# Revit family: MA551
name_source: partatom
category: Communication Devices
revit_build: Autodesk Revit 2018 (Build: 20170223_1515(x64)
units: mm (PartAtom-declared; Revit-internal decimal feet)

## family parameters
Always vertical = Yes
Cut with Voids When Loaded = No
Maintain Annotation Orientation = No
Part Type = Normal
Room Calculation Point = No
Round Connector Dimension = Use Diameter
Shared = No
Work Plane-Based = No

## types (1)
- MA551
    CONNECTIVITY - Input Terminals - Data = USB 2.0 x 2 (5V/2A, FW), USB Type B (Software)
    CONNECTIVITY - Input Terminals - Digital = HDMI 2.0 x 2, DP 1.4 x 2.4
    CONNECTIVITY - Input Terminals - External Control = LAN (100Mbit), 3.5mm Mini Jack IR Remote, RS-232C
    CONNECTIVITY - Output Terminals - Audio = 3.5mm Mini Jack, External Speaker Jack (15W x 2)
    CONNECTIVITY - Output Terminals - Digital = HDMI x 1, DisplayPort x 1
    CONNECTIVITY - Output Terminals - External Control = LAN (100Mbit)
    Description = NEC MultiSync MA Series Large Format Displays
    ENVIRONMENTAL CONDITIONS- Operating Altitude" = 3000m (9843ft
    ENVIRONMENTAL CONDITIONS- Operating Humidity = 20-80%
    ENVIRONMENTAL CONDITIONS- Operating Temperature = 0 to 40C
    LCD MODULE- Aspect Ratio = 16 : 9
    LCD MODULE- Brightness (Typical/Minimum) = 500  cd/m2
    LCD MODULE- Color Gamut = 86% DCI
    LCD MODULE- Contrast Ratio (typical) = >= 8000 : 1
    LCD MODULE- Displayable Colors = Over 1.07 Billion (10bit)
    LCD MODULE- Native Resolution = 3840 x 2160
    LCD MODULE- Orientation = Landscape and Portrait (CCW Rotation)
    LCD MODULE- Panel Haze (%) = 28
    LCD MODULE- Panel Technology = IPS
    LCD MODULE- Viewable Image Size = 55 inches
    LCD MODULE- Viewing Angle (typical) = 178deg Vert., 178deg Hor. (89U/89D/89L/89R) @ CR>10
    Manufacturer = NEC Display Solutions
    Model = MA551
    PHYSICAL SPECS- Net Dimensions (w/o Stand. W x H x D) = 48.8 x 28.1 x 2.4 in. (1239.6 x 713.0 x 60.9 mm)
    PHYSICAL SPECS- Net Weight (w/o Stand) = 27.6 kg / 60.8 lbs
    POWER CONSUMPTION- Current Rating = 2.8A - 1.2A @ 100V - 240V
    POWER CONSUMPTION- On (Typ/Max Brightness/All Max) = 90W / 110W / 255W
    URL = www.necdisplay.com

## geometry (parser evidence)
native form markers: Sweep x2
no freeform markers — native parametric forms only
